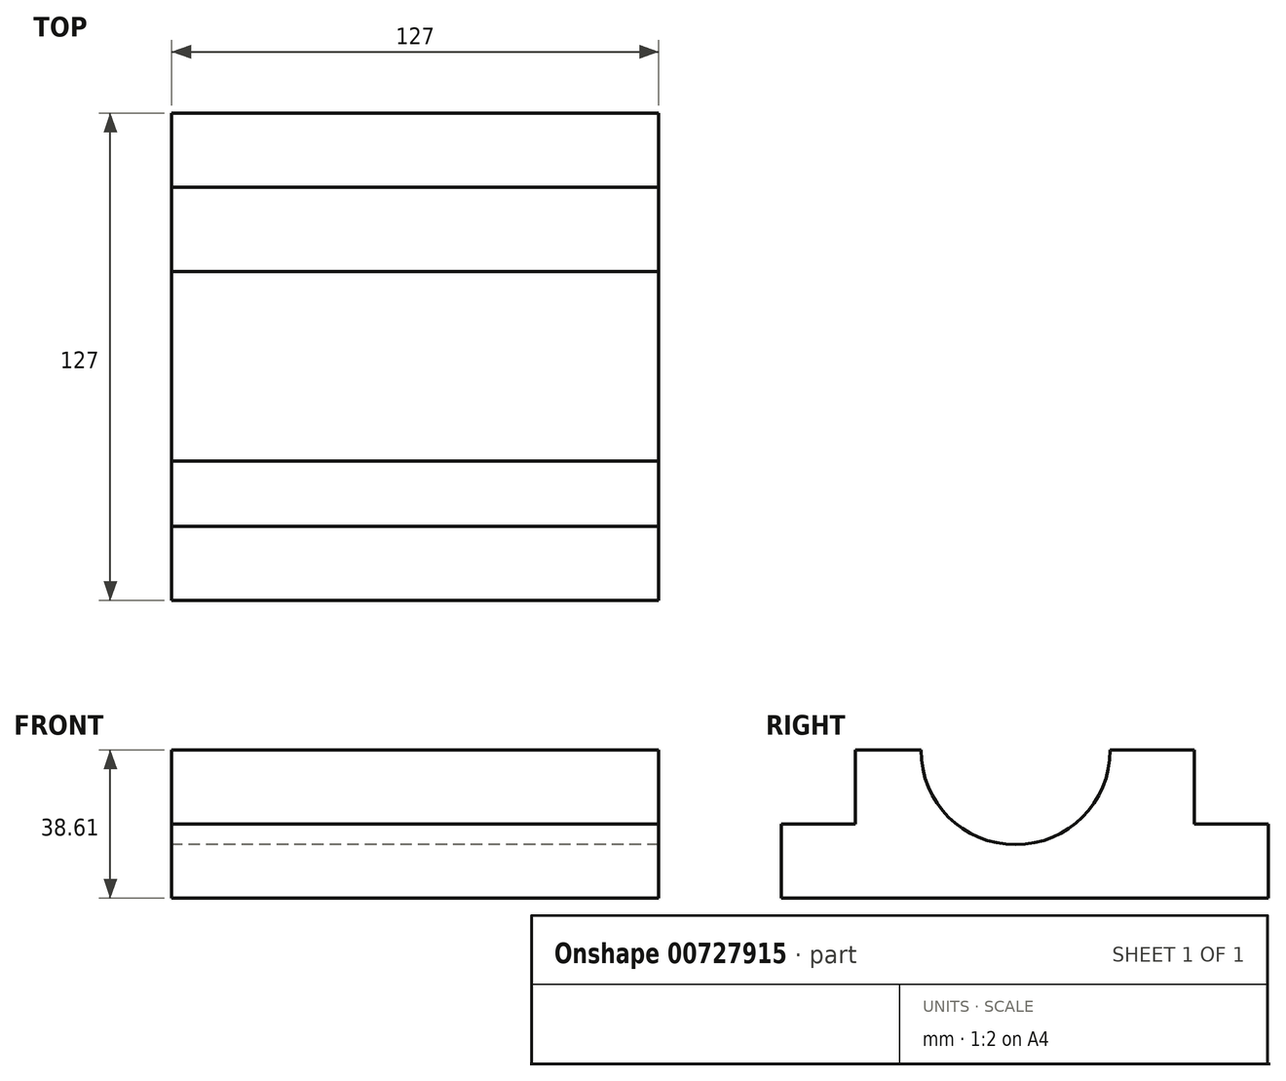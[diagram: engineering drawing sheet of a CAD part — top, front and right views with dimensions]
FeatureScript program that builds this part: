
annotation { "Feature Type Name" : "Feature", "Feature Type Description" : "" }
export const myFeature = defineFeature(function(context is Context, id is Id, definition is map)
    precondition{}
    {
        {
            var Q0;
            Q0=qCreatedBy(makeId("Right.planeOp"),FACE);
            var sketch = newSketch(context, id + "F0", { "sketchPlane" : qUnion([Q0])});
            skLineSegment(sketch, "E0", {"start": v(-61.05, -19.3) * mm, "end": v(-61.05, -38.6) * mm});
            skLineSegment(sketch, "E1", {"start": v(-61.05, -38.6) * mm, "end": v(65.95, -38.6) * mm});
            skLineSegment(sketch, "E2", {"start": v(65.95, -38.6) * mm, "end": v(65.95, -19.3) * mm});
            skLineSegment(sketch, "E3", {"start": v(-61.05, -19.3) * mm, "end": v(-41.74, -19.3) * mm});
            skLineSegment(sketch, "E4", {"start": v(65.95, -19.3) * mm, "end": v(46.65, -19.3) * mm});
            skLineSegment(sketch, "E5", {"start": v(-41.74, -19.3) * mm, "end": v(-41.74, 0) * mm});
            skLineSegment(sketch, "E6", {"start": v(46.65, -19.3) * mm, "end": v(46.65, 0) * mm});
            skLineSegment(sketch, "E7", {"start": v(-41.74, 0) * mm, "end": v(-35.14, 0) * mm});
            skLineSegment(sketch, "E8", {"start": v(46.65, 0) * mm, "end": v(40.05, 0) * mm});
            skCircle(sketch, "E9", {"center": v(0, 0) * mm, "radius": 24.69 * mm});
            skLineSegment(sketch, "E10", {"start": v(-35.14, 0) * mm, "end": v(-24.69, 0) * mm});
            skLineSegment(sketch, "E11", {"start": v(40.05, 0) * mm, "end": v(24.69, 0) * mm});
            skSolve(sketch);
        }
        {
            var Q0;
            Q0=makeQuery(id+"F0.imprint","IMPRINT",FACE,{"disambiguationData":[TD([[makeQuery(id+"F0.imprint","IMPRINT",EDGE,{"derivedFrom":sQuery(id+"F0.wireOp",EDGE,"E0")}),1.0]])]});
            extrude(context, id + "F1", {"entities" : qUnion([Q0]), "depth" : 127 * mm, "offsetDistance" : 25.4 * mm});
        }
    });
